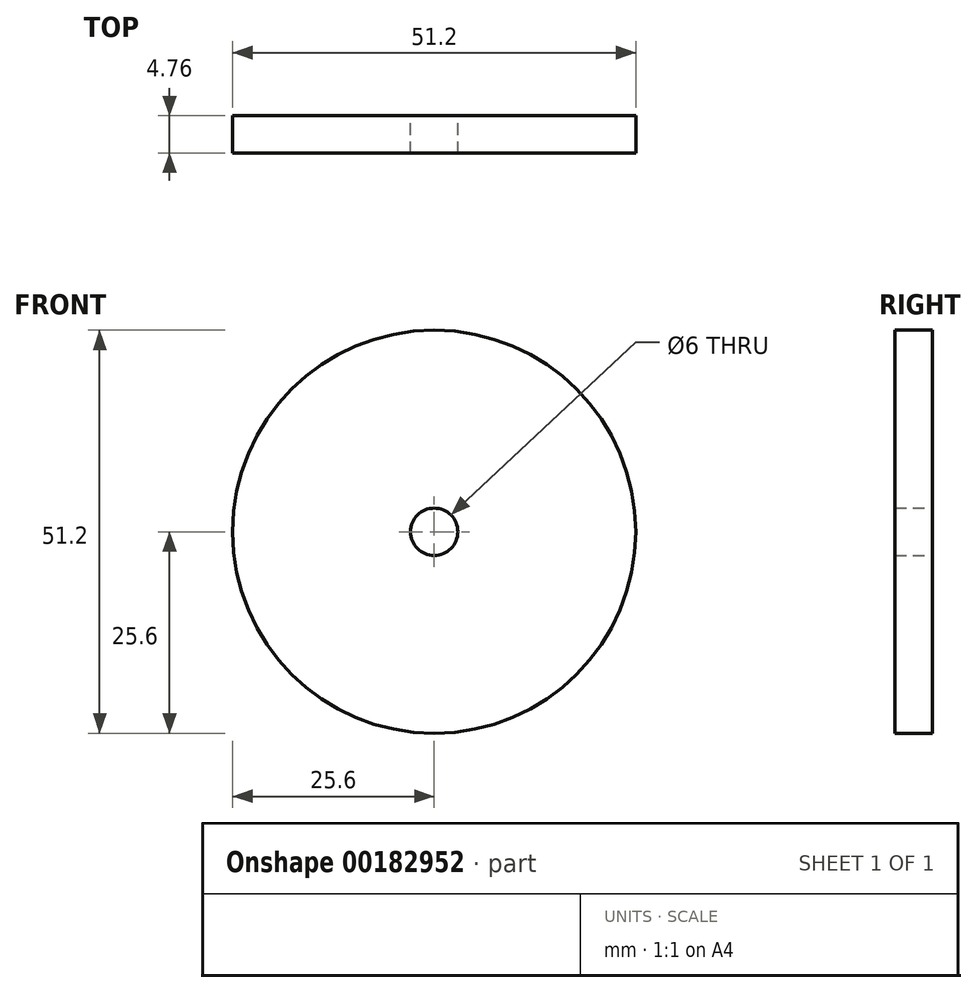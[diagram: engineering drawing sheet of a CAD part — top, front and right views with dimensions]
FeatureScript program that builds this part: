
annotation { "Feature Type Name" : "Feature", "Feature Type Description" : "" }
export const myFeature = defineFeature(function(context is Context, id is Id, definition is map)
    precondition{}
    {
        {
            var Q0;
            Q0=qCreatedBy(makeId("Front.planeOp"),FACE);
            var sketch = newSketch(context, id + "F0", { "sketchPlane" : qUnion([Q0])});
            skCircle(sketch, "E0", {"center": v(0, 0) * mm, "radius": 25.6 * mm});
            skCircle(sketch, "E1", {"center": v(0, 0) * mm, "radius": 3 * mm});
            skSolve(sketch);
        }
        {
            var Q0;
            Q0=makeQuery(id+"F0.imprint","IMPRINT",FACE,{"disambiguationData":[TD([[makeQuery(id+"F0.imprint","IMPRINT",EDGE,{"derivedFrom":sQuery(id+"F0.wireOp",EDGE,"E0")}),1.0]])]});
            var Q1;
            Q1=sQuery(id+"F0.wireOp",EDGE,"E1");
            var Q2;
            Q2=sQuery(id+"F0.wireOp",EDGE,"E0");
            extrude(context, id + "F1", {"entities" : qUnion([Q0]), "surfaceEntities" : qUnion([Q1, Q2]), "depth" : 4.76 * mm});
        }
    });
